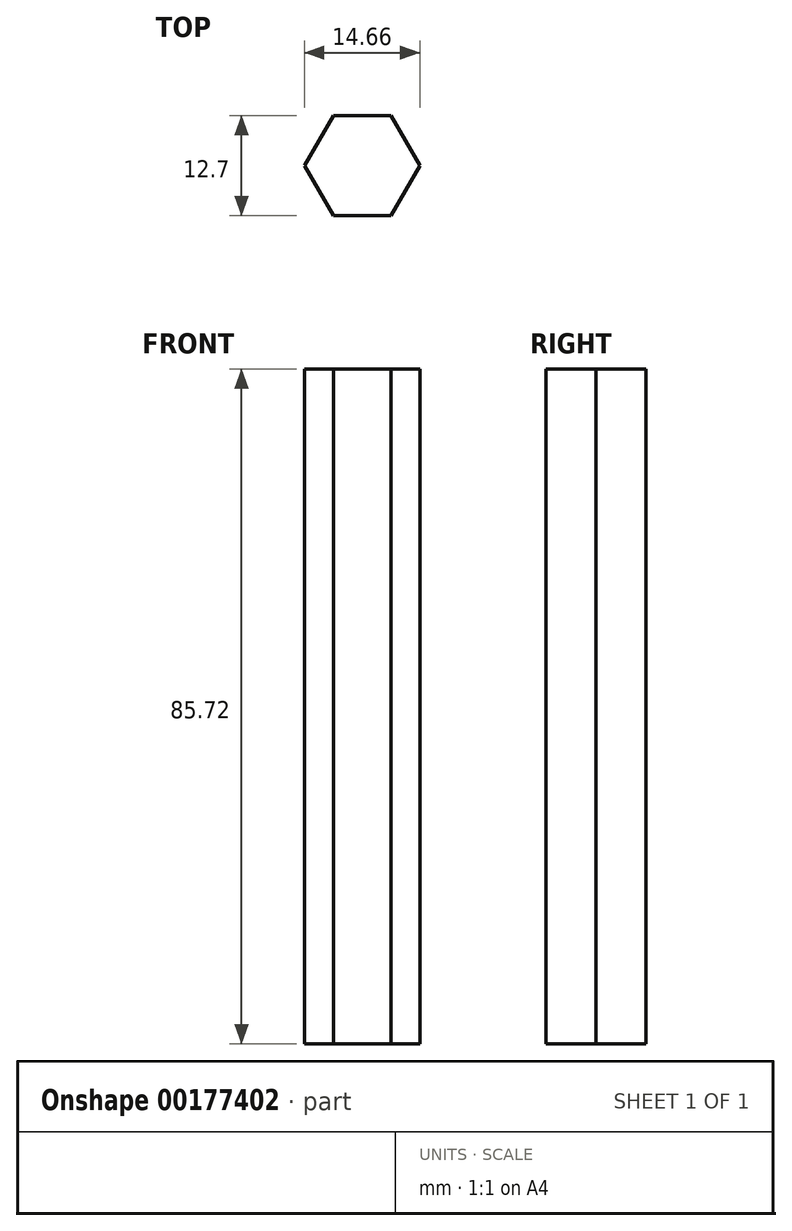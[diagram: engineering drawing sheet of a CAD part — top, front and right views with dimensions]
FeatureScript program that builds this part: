
annotation { "Feature Type Name" : "Feature", "Feature Type Description" : "" }
export const myFeature = defineFeature(function(context is Context, id is Id, definition is map)
    precondition{}
    {
        {
            var Q0;
            Q0=qCreatedBy(makeId("Top.planeOp"),FACE);
            var sketch = newSketch(context, id + "F0", { "sketchPlane" : qUnion([Q0])});
            skCircle(sketch, "E0", {"center": v(0, 0) * mm, "radius": 6.35 * mm});
            skCircle(sketch, "E1.cCircle", {"center": v(0, 0) * mm, "radius": 6.35 * mm, "construction": true});
            skLineSegment(sketch, "E1.0", {"start": v(-3.67, 6.35) * mm, "end": v(3.67, 6.35) * mm});
            skLineSegment(sketch, "E1.1", {"start": v(3.67, 6.35) * mm, "end": v(7.33, 0) * mm});
            skLineSegment(sketch, "E1.2", {"start": v(7.33, 0) * mm, "end": v(3.67, -6.35) * mm});
            skLineSegment(sketch, "E1.3", {"start": v(3.67, -6.35) * mm, "end": v(-3.67, -6.35) * mm});
            skLineSegment(sketch, "E1.4", {"start": v(-3.67, -6.35) * mm, "end": v(-7.33, 0) * mm});
            skLineSegment(sketch, "E1.5", {"start": v(-7.33, 0) * mm, "end": v(-3.67, 6.35) * mm});
            skPoint(sketch, "E1.0.midPoint", {"position": v(0, 6.35) * mm});
            skSolve(sketch);
        }
        {
            var Q0;
            Q0 = qSketchRegion(id + "F0", true);
            extrude(context, id + "F1", {"entities" : qUnion([Q0]), "depth" : 85.72 * mm});
        }
    });
